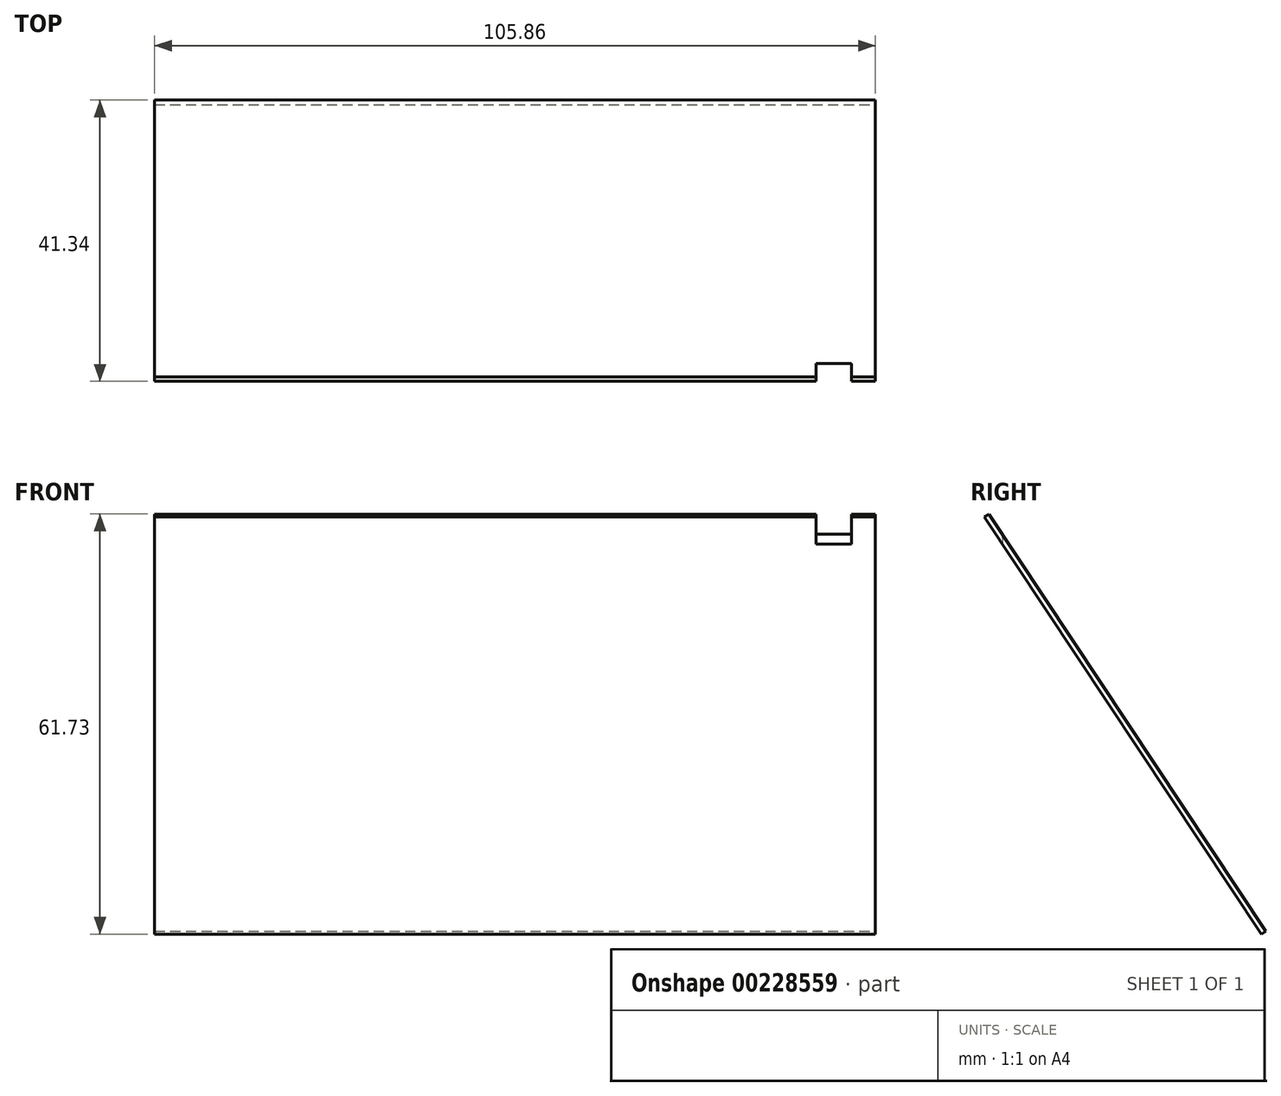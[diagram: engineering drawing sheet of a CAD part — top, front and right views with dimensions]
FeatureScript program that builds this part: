
annotation { "Feature Type Name" : "Feature", "Feature Type Description" : "" }
export const myFeature = defineFeature(function(context is Context, id is Id, definition is map)
    precondition{}
    {
        {
            var Q0;
            Q0=qCreatedBy(makeId("Right.planeOp"),FACE);
            var sketch = newSketch(context, id + "F0", { "sketchPlane" : qUnion([Q0])});
            skLineSegment(sketch, "E0", {"start": v(2933.7, 6096) * mm, "end": v(3543.3, 5177.64) * mm});
            skLineSegment(sketch, "E1", {"start": v(2933.7, 6096) * mm, "end": v(0, 10515.6) * mm});
            skSolve(sketch);
        }
        {
            var Q0;
            Q0=sQuery(id+"F0.wireOp",EDGE,"E1");
            var Q1;
            Q1=sQuery(id+"F0.wireOp",EDGE,"E0");
            extrude(context, id + "F1", {"bodyType" : ToolBodyType.SURFACE, "surfaceEntities" : qUnion([Q0, Q1]), "endBound" : BoundingType.SYMMETRIC, "depth" : 9220.2 * mm});
        }
        {
            var Q0;
            Q0=makeQuery(id+"F1.opExtrude","SWEPT_FACE",FACE,{"disambiguationData":[OSD([sQuery(id+"F0.wireOp",EDGE,"paPBDd7v-Khaj-EFFU-Sq9n-Kob8jBGrBa6K"),sQuery(id+"F0.wireOp",EDGE,"E0")])]});
            extrude(context, id + "F2", {"entities" : qUnion([Q0]), "depth" : 69.14 * mm});
        }
        {
            var Q0;
            Q0=makeQuery(id+"F2.opExtrude","SWEPT_BODY",BODY,{"disambiguationData":[OSD([sQuery(id+"F0.wireOp",EDGE,"E0"),sQuery(id+"F0.wireOp",EDGE,"E1")])]});
            var Q1;
            Q1=makeQuery(id+"F1.opExtrude","SWEPT_BODY",BODY,{"disambiguationData":[OSD([sQuery(id+"F0.wireOp",EDGE,"E0"),sQuery(id+"F0.wireOp",EDGE,"E1")])]});
            var Q2;
            Q2=qCreatedBy(makeId("Origin.pointOp"),VERTEX);
            transform(context, id + "F3", {"entities" : qUnion([Q0, Q1]), "transformType" : TransformType.SCALE_UNIFORMLY, "scale" : 1 / 87.1, "scalePoint" : qUnion([Q2]), "makeCopy" : false});
        }
        {
            var Q0;
            {var subQ0=sQuery(id+"F0.wireOp",EDGE,"E1");var subQ1=sQuery(id+"F0.wireOp",EDGE,"E0");Q0=makeQuery(id+"F2.opExtrude","SWEPT_FACE",FACE,{"disambiguationData":[OSD([subQ1,subQ0]),TDD([makeQuery(id+"F1.opExtrude","CAP_EDGE",EDGE,{"disambiguationData":[OSD([subQ1,subQ0])],"isStart":false})])]});}
            cPlane(context, id + "F4", {"entities" : qUnion([Q0]), "cplaneType" : CPlaneType.OFFSET, "offset" : 8.75 * mm, "oppositeDirection" : true, "width" : 152.4 * mm, "height" : 152.4 * mm});
        }
        {
            var Q0;
            Q0=qCreatedBy(id+"F4.planeOp",FACE);
            var sketch = newSketch(context, id + "F5", { "sketchPlane" : qUnion([Q0])});
            skLineSegment(sketch, "E2.bottom", {"start": v(-2.62, 121.17) * mm, "end": v(2.62, 121.17) * mm});
            skLineSegment(sketch, "E2.top", {"start": v(-2.62, 107.4) * mm, "end": v(2.62, 107.4) * mm});
            skLineSegment(sketch, "E2.left", {"start": v(-2.62, 121.17) * mm, "end": v(-2.62, 107.4) * mm});
            skLineSegment(sketch, "E2.right", {"start": v(2.62, 121.17) * mm, "end": v(2.62, 107.4) * mm});
            skSolve(sketch);
        }
        {
            var Q0;
            Q0=makeQuery(id+"F5.imprint","IMPRINT",FACE,{"disambiguationData":[TD([[makeQuery(id+"F5.imprint","IMPRINT",EDGE,{"derivedFrom":sQuery(id+"F5.wireOp",EDGE,"E2.bottom")}),-1.0]])]});
            extrude(context, id + "F6", {"entities" : qUnion([Q0]), "operationType" : NewBodyOperationType.REMOVE, "depth" : 5.25 * mm});
        }
    });
